# Revit family: Faucet-Kitchen-KOHLER-Forte-K-10415
name_source: partatom
category: Plumbing Fixtures
revit_build: Autodesk Revit 2017 (Build: 20160225_1515(x64)
units: mm (PartAtom-declared; Revit-internal decimal feet)

## family parameters
Cut with Voids When Loaded = No
Host = Face
OmniClass Number = 23.31.11.00
OmniClass Title = Faucets
Part Type = Normal
Room Calculation Point = No
Round Connector Dimension = Use Diameter
Shared = No

## types (3) — shared parameters
ADA Compliant = Yes
Assembly Code = D2010
CW Connection = Yes
Cold Water Inlet = Cold Water Inlet
Date Modified = 10/21/2020
Default Elevation = 36"
Description = Single-hole kitchen sink faucet with 9-1/16 spout
Drain Included = No
Flow Rate = 2 GPM
HW Connection = Yes
Handle Clearance = 3 3/4"
Height = 8 7/8"
Hot Water Inlet = Hot Water Inlet
Length = 9 1/16"
Manufacturer = KOHLER Co.
Master Format 2014 = 22 41 39
Master Format 2014 Name = Residential Faucets, Supplies, and Trim
Material = Premium Metal Construction
Pressure = 60.00 psi
Product Documentation Link = https://www.us.kohler.com
Product Name = Forte
Product Page URL = http://www.us.kohler.com
Spout Reach = 9 1/16"
URL = https://www.us.kohler.com
Vent Connection = No
Waste Connection = No
Waste Water Outlet = Waste Water Outlet
WaterSense Certified = No
Width = 2"

## per-type parameters (varying)
| type | Finish | Model | Type |
| CP- Polished Chrome | Kohler-Metal-CP-Polished_Chrome | K-10415-CP | 1 |
| BN- Brushed Nickel | Kohler-Metal-BN-Vibrant_Brushed_Nickel | K-10415-BN | 2 |
| VS- Vibrant Stainless | Kohler-Metal-VS-Vibrant_Stainless | K-10415-VS | 3 |

## geometry (parser evidence)
native form markers: Sweep x5
no freeform markers — native parametric forms only
